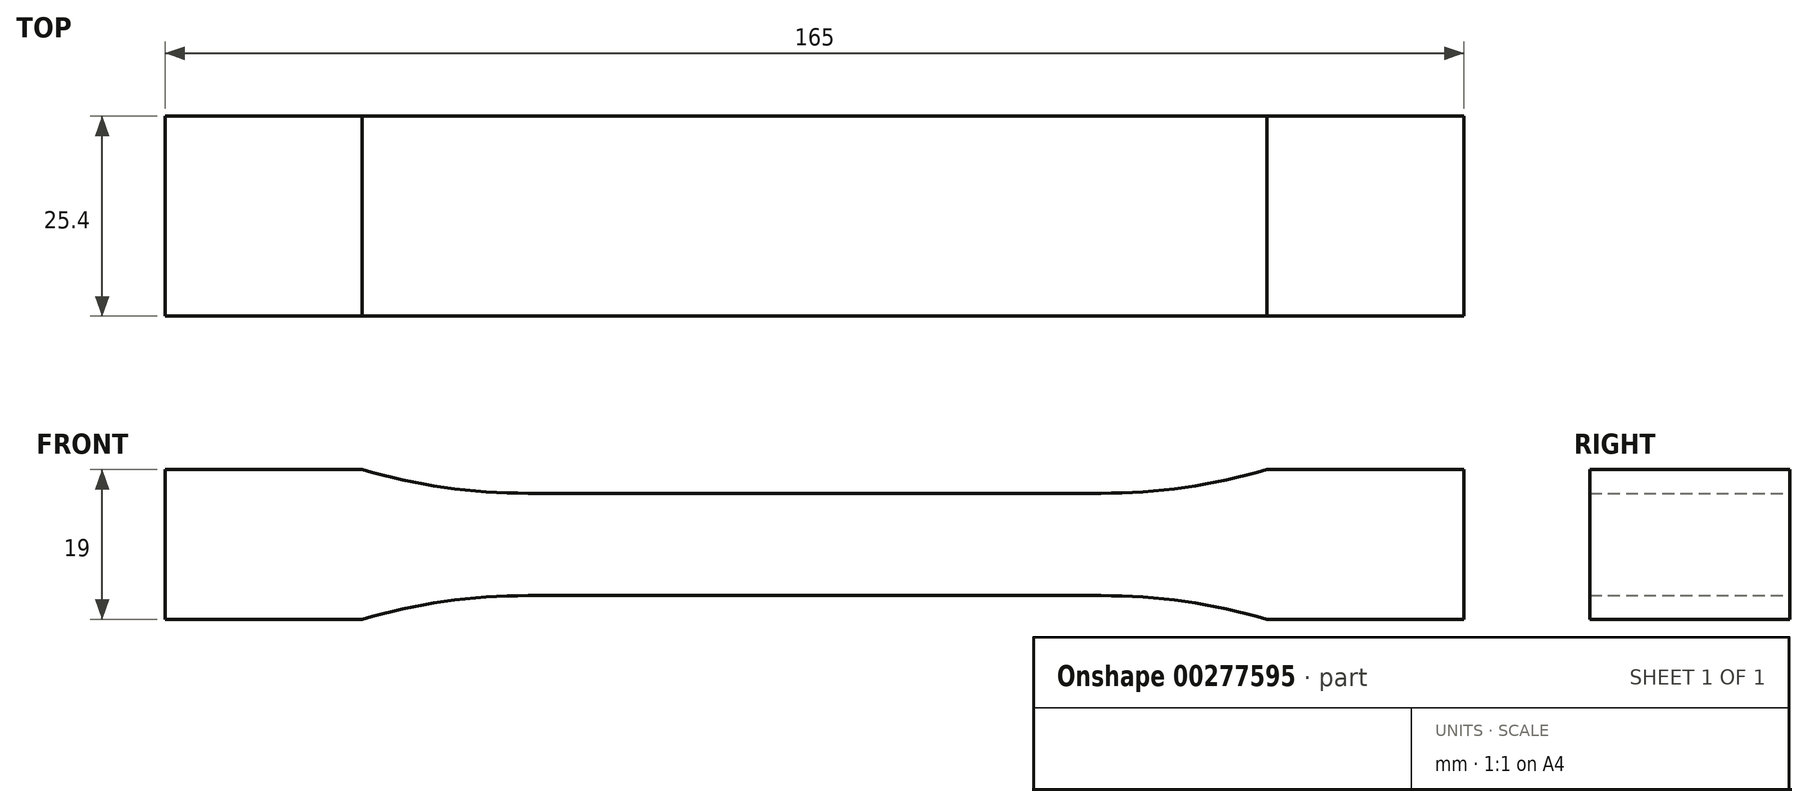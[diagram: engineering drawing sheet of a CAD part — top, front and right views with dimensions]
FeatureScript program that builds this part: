
annotation { "Feature Type Name" : "Feature", "Feature Type Description" : "" }
export const myFeature = defineFeature(function(context is Context, id is Id, definition is map)
    precondition{}
    {
        {
            var Q0;
            Q0=qCreatedBy(makeId("Front.planeOp"),FACE);
            var sketch = newSketch(context, id + "F0", { "sketchPlane" : qUnion([Q0])});
            skLineSegment(sketch, "E0", {"start": v(0, 6.5) * mm, "end": v(36.36, 6.5) * mm});
            skArc(sketch, "E1", {"start": v(36.36, 6.5) * mm, "mid": v(47.03, 7.25) * mm, "end": v(57.5, 9.5) * mm});
            skLineSegment(sketch, "E2", {"start": v(57.5, 9.5) * mm, "end": v(82.5, 9.5) * mm});
            skLineSegment(sketch, "E3.MirrorCS", {"start": v(57.5, -9.5) * mm, "end": v(82.5, -9.5) * mm});
            skLineSegment(sketch, "E4.MirrorCS", {"start": v(0, -6.5) * mm, "end": v(36.36, -6.5) * mm});
            skArc(sketch, "E5.MirrorCS", {"start": v(36.36, -6.5) * mm, "mid": v(47.03, -7.25) * mm, "end": v(57.5, -9.5) * mm});
            skArc(sketch, "E6.MirrorCS", {"start": v(-36.36, -6.5) * mm, "mid": v(-47.03, -7.25) * mm, "end": v(-57.5, -9.5) * mm});
            skLineSegment(sketch, "E7.MirrorCS", {"start": v(0, 6.5) * mm, "end": v(-36.36, 6.5) * mm});
            skArc(sketch, "E8.MirrorCS", {"start": v(-36.36, 6.5) * mm, "mid": v(-47.03, 7.25) * mm, "end": v(-57.5, 9.5) * mm});
            skLineSegment(sketch, "E9.MirrorCS", {"start": v(-57.5, -9.5) * mm, "end": v(-82.5, -9.5) * mm});
            skLineSegment(sketch, "E10.MirrorCS", {"start": v(0, -6.5) * mm, "end": v(-36.36, -6.5) * mm});
            skLineSegment(sketch, "E11.MirrorCS", {"start": v(-57.5, 9.5) * mm, "end": v(-82.5, 9.5) * mm});
            skLineSegment(sketch, "E12", {"start": v(-82.5, 9.5) * mm, "end": v(-82.5, -9.5) * mm});
            skLineSegment(sketch, "E13", {"start": v(82.5, 9.5) * mm, "end": v(82.5, -9.5) * mm});
            skSolve(sketch);
        }
        {
            var Q0;
            Q0 = qSketchRegion(id + "F0", true);
            extrude(context, id + "F1", {"entities" : qUnion([Q0]), "depth" : 25.4 * mm});
        }
    });
